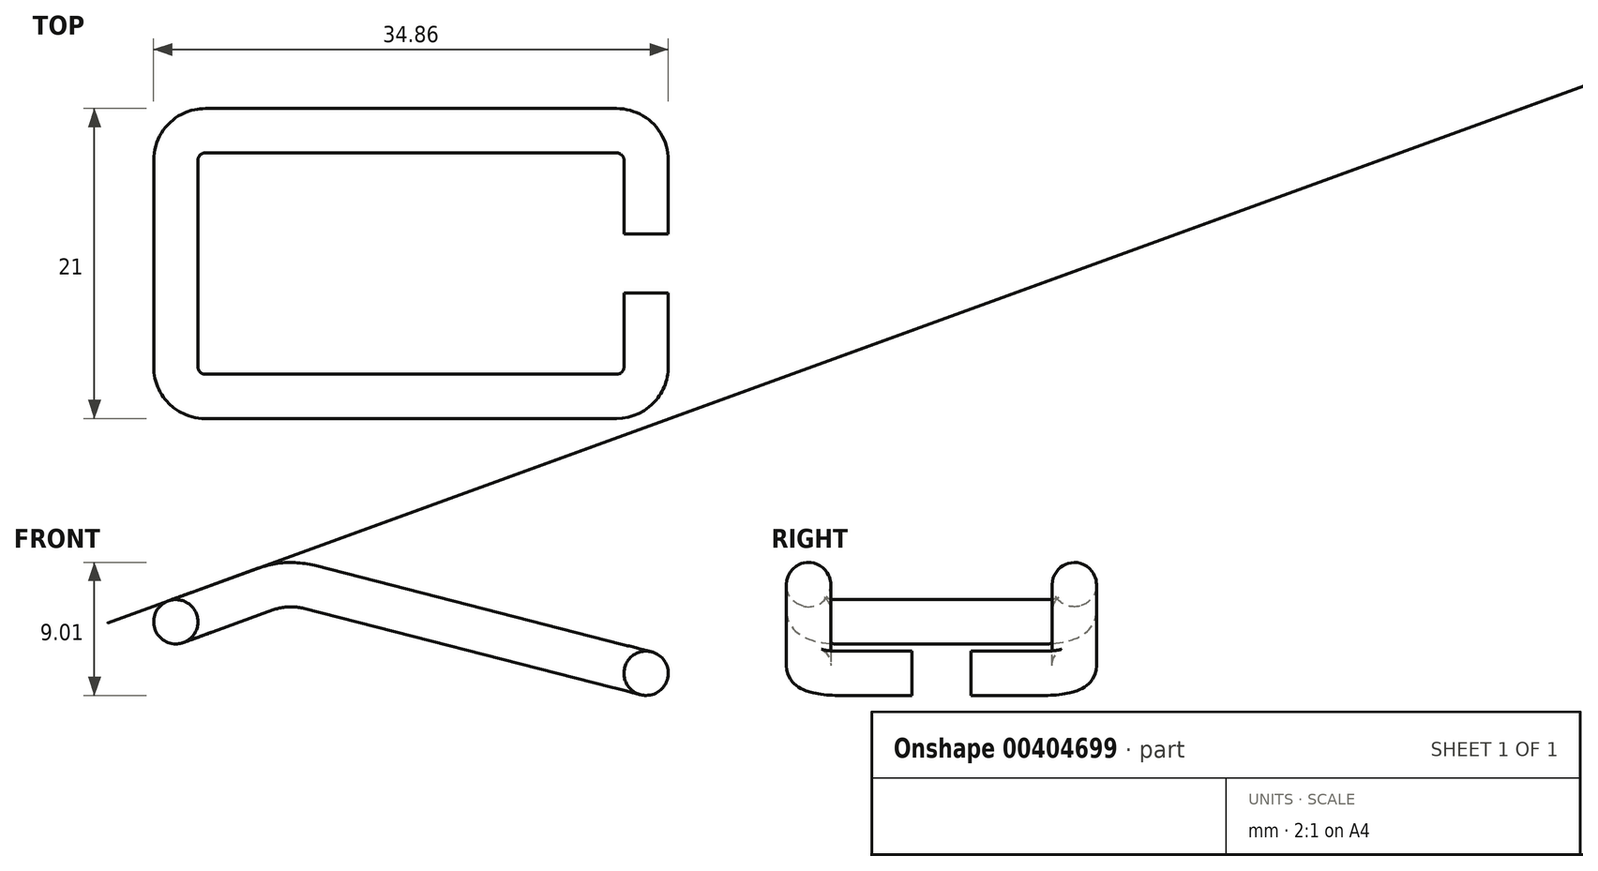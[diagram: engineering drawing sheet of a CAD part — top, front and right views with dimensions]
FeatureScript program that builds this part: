
annotation { "Feature Type Name" : "Feature", "Feature Type Description" : "" }
export const myFeature = defineFeature(function(context is Context, id is Id, definition is map)
    precondition{}
    {
        {
            var Q0;
            Q0=qCreatedBy(makeId("Front.planeOp"),FACE);
            var sketch = newSketch(context, id + "F0", { "sketchPlane" : qUnion([Q0])});
            skLineSegment(sketch, "E0", {"start": v(-7.54, 3.5) * mm, "end": v(0, 6.23) * mm});
            skLineSegment(sketch, "E1", {"start": v(24.32, 0) * mm, "end": v(0, 6.23) * mm});
            skPoint(sketch, "E2.orphan", {"position": v(24.8, -0.12) * mm});
            skLineSegment(sketch, "E3", {"start": v(24.32, 0) * mm, "end": v(-7.54, 0) * mm});
            skLineSegment(sketch, "E4", {"start": v(-7.54, 0) * mm, "end": v(-7.54, 3.5) * mm});
            skSolve(sketch);
        }
        {
            var Q0;
            Q0=makeQuery(id+"F0.imprint","IMPRINT",FACE,{"disambiguationData":[TD([[makeQuery(id+"F0.imprint","IMPRINT",EDGE,{"derivedFrom":sQuery(id+"F0.wireOp",EDGE,"E0")}),-1.0]])]});
            extrude(context, id + "F1", {"entities" : qUnion([Q0]), "oppositeDirection" : true, "depth" : 18 * mm, "symmetric" : true});
        }
        {
            var Q0;
            Q0=makeQuery(id+"F1.opExtrude","SWEPT_FACE",FACE,{"disambiguationData":[OSD([sQuery(id+"F0.wireOp",EDGE,"E1")])]});
            var sketch = newSketch(context, id + "F2", { "sketchPlane" : qUnion([Q0])});
            skLineSegment(sketch, "E5.bottom", {"start": v(21.7, 2) * mm, "end": v(25.41, 2) * mm});
            skLineSegment(sketch, "E5.top", {"start": v(21.7, -2) * mm, "end": v(25.41, -2) * mm});
            skLineSegment(sketch, "E5.left", {"start": v(21.7, 2) * mm, "end": v(21.7, -2) * mm});
            skLineSegment(sketch, "E5.right", {"start": v(25.41, 2) * mm, "end": v(25.41, -2) * mm});
            skPoint(sketch, "E5.middle", {"position": v(23.56, 0) * mm});
            skSolve(sketch);
        }
        {
            var Q0;
            Q0 = qSketchRegion(id + "F2", true);
            extrude(context, id + "F3", {"entities" : qUnion([Q0]), "operationType" : NewBodyOperationType.REMOVE, "endBound" : BoundingType.THROUGH_ALL, "oppositeDirection" : true, "depth" : 25 * mm});
        }
        {
            var Q0;
            Q0=makeQuery(id+"F3.boolean.opBoolean","COPY",FACE,{"derivedFrom":makeQuery(id+"F3.opExtrude","SWEPT_FACE",FACE,{"disambiguationData":[OSD([sQuery(id+"F2.wireOp",EDGE,"E5.bottom")])]})});
            var sketch = newSketch(context, id + "F4", { "sketchPlane" : qUnion([Q0])});
            skPoint(sketch, "E6.0", {"position": v(24.32, 0) * mm});
            skCircle(sketch, "E7", {"center": v(24.32, 0) * mm, "radius": 1.5 * mm});
            skSolve(sketch);
        }
        {
            var Q0;
            Q0=makeQuery(id+"F1.opExtrude","SWEPT_FACE",FACE,{"disambiguationData":[OSD([sQuery(id+"F0.wireOp",EDGE,"E3")])]});
            extrude(context, id + "F5", {"entities" : qUnion([Q0]), "operationType" : NewBodyOperationType.ADD, "depth" : 5 * mm});
        }
        {
            var Q0;
            Q0=makeQuery(id+"F1.opExtrude","SWEPT_EDGE",EDGE,{"disambiguationData":[OSD([sQuery(id+"F0.wireOp",EDGE,"E0"),sQuery(id+"F0.wireOp",EDGE,"E1")])]});
            fillet(context, id + "F6", {"entities" : qUnion([Q0]), "radius" : 5 * mm, "tangentPropagation" : true, "allowEdgeOverflow" : false});
        }
        {
            var Q0;
            Q0=makeQuery(id+"F1.opExtrude","CAP_EDGE",EDGE,{"disambiguationData":[OSD([sQuery(id+"F0.wireOp",EDGE,"E4")])],"isStart":true});
            var Q1;
            Q1=makeQuery(id+"F1.opExtrude","CAP_EDGE",EDGE,{"disambiguationData":[OSD([sQuery(id+"F0.wireOp",EDGE,"E4")])],"isStart":false});
            var Q2;
            {var subQ0=sQuery(id+"F0.wireOp",EDGE,"E3");var subQ1=sQuery(id+"F0.wireOp",EDGE,"E1");Q2=makeQuery(id+"F5.opExtrude","SWEPT_EDGE",EDGE,{"disambiguationData":[OSD([subQ1,subQ0]),TDD([makeQuery(id+"F1.opExtrude","CAP_VERTEX",VERTEX,{"disambiguationData":[OSD([subQ1,subQ0])],"isStart":true})])]});}
            var Q3;
            {var subQ0=sQuery(id+"F0.wireOp",EDGE,"E3");var subQ1=sQuery(id+"F0.wireOp",EDGE,"E1");Q3=makeQuery(id+"F5.opExtrude","SWEPT_EDGE",EDGE,{"disambiguationData":[OSD([subQ1,subQ0]),TDD([makeQuery(id+"F1.opExtrude","CAP_VERTEX",VERTEX,{"disambiguationData":[OSD([subQ1,subQ0])],"isStart":false})])]});}
            fillet(context, id + "F7", {"entities" : qUnion([Q0, Q1, Q2, Q3]), "radius" : 2 * mm, "tangentPropagation" : true, "allowEdgeOverflow" : false});
        }
        {
            var Q0;
            Q0 = qSketchRegion(id + "F4", true);
            var Q1;
            {var subQ0=sQuery(id+"F0.wireOp",EDGE,"E3");var subQ1=sQuery(id+"F0.wireOp",EDGE,"E1");var subQ2=makeQuery(id+"F3.boolean.opBoolean","SPLIT",EDGE,{"disambiguationData":[TD([makeQuery(id+"F3.opExtrude","SWEPT_FACE",FACE,{"disambiguationData":[OSD([sQuery(id+"F2.wireOp",EDGE,"E5.bottom")])]})])],"derivedFrom":makeQuery(id+"F1.opExtrude","SWEPT_EDGE",EDGE,{"disambiguationData":[OSD([subQ1,subQ0])]})});Q1=makeQuery(id+"F5.boolean.opBoolean","MERGE",EDGE,{"derivedFrom":[subQ2,makeQuery(id+"F5.opExtrude","CAP_EDGE",EDGE,{"disambiguationData":[OSD([subQ1,subQ0]),TDD([subQ2])],"isStart":true})]});}
            var Q2;
            {var subQ0=sQuery(id+"F0.wireOp",EDGE,"E1");var subQ1=sQuery(id+"F0.wireOp",EDGE,"E3");Q2=makeQuery(id+"F7.opFillet","BLEND_EDGE",EDGE,{"blendedFrom":[makeQuery(id+"F5.opExtrude","SWEPT_EDGE",EDGE,{"disambiguationData":[OSD([subQ0,subQ1]),TDD([makeQuery(id+"F1.opExtrude","CAP_VERTEX",VERTEX,{"disambiguationData":[OSD([subQ0,subQ1])],"isStart":false})])]}),makeQuery(id+"F1.opExtrude","SWEPT_FACE",FACE,{"disambiguationData":[OSD([subQ0])]})],"blendedInto":[makeQuery(id+"F1.opExtrude","SWEPT_FACE",FACE,{"disambiguationData":[OSD([subQ0])]})]});}
            var Q3;
            Q3=makeQuery(id+"F1.opExtrude","CAP_EDGE",EDGE,{"disambiguationData":[OSD([sQuery(id+"F0.wireOp",EDGE,"E1")])],"isStart":false});
            var Q4;
            {var subQ0=sQuery(id+"F0.wireOp",EDGE,"E3");var subQ1=sQuery(id+"F0.wireOp",EDGE,"E1");var subQ2=sQuery(id+"F0.wireOp",EDGE,"E0");Q4=makeQuery(id+"F6.opFillet","BLEND_EDGE",EDGE,{"blendedFrom":[makeQuery(id+"F1.opExtrude","SWEPT_EDGE",EDGE,{"disambiguationData":[OSD([subQ2,subQ1])]}),makeQuery(id+"F5.boolean.opBoolean","MERGE",FACE,{"derivedFrom":[makeQuery(id+"F1.opExtrude","CAP_FACE",FACE,{"disambiguationData":[OSD([subQ2,subQ1,subQ0,sQuery(id+"F0.wireOp",EDGE,"E4")])],"isStart":false}),makeQuery(id+"F5.opExtrude","SWEPT_FACE",FACE,{"disambiguationData":[OSD([subQ0]),TDD([makeQuery(id+"F1.opExtrude","CAP_EDGE",EDGE,{"disambiguationData":[OSD([subQ0])],"isStart":false})])]})]})],"blendedInto":[makeQuery(id+"F5.boolean.opBoolean","MERGE",FACE,{"derivedFrom":[makeQuery(id+"F1.opExtrude","CAP_FACE",FACE,{"disambiguationData":[OSD([subQ2,subQ1,subQ0,sQuery(id+"F0.wireOp",EDGE,"E4")])],"isStart":false}),makeQuery(id+"F5.opExtrude","SWEPT_FACE",FACE,{"disambiguationData":[OSD([subQ0]),TDD([makeQuery(id+"F1.opExtrude","CAP_EDGE",EDGE,{"disambiguationData":[OSD([subQ0])],"isStart":false})])]})]})]});}
            var Q5;
            Q5=makeQuery(id+"F1.opExtrude","CAP_EDGE",EDGE,{"disambiguationData":[OSD([sQuery(id+"F0.wireOp",EDGE,"E0")])],"isStart":false});
            var Q6;
            {var subQ0=sQuery(id+"F0.wireOp",EDGE,"E4");var subQ1=sQuery(id+"F0.wireOp",EDGE,"E3");Q6=makeQuery(id+"F7.opFillet","BLEND_EDGE",EDGE,{"blendedFrom":[makeQuery(id+"F5.boolean.opBoolean","MERGE",EDGE,{"derivedFrom":[makeQuery(id+"F1.opExtrude","CAP_EDGE",EDGE,{"disambiguationData":[OSD([subQ0])],"isStart":false}),makeQuery(id+"F5.opExtrude","SWEPT_EDGE",EDGE,{"disambiguationData":[OSD([subQ1,subQ0]),TDD([makeQuery(id+"F1.opExtrude","CAP_VERTEX",VERTEX,{"disambiguationData":[OSD([subQ1,subQ0])],"isStart":false})])]})]}),makeQuery(id+"F1.opExtrude","SWEPT_FACE",FACE,{"disambiguationData":[OSD([sQuery(id+"F0.wireOp",EDGE,"E0")])]})],"blendedInto":[makeQuery(id+"F1.opExtrude","SWEPT_FACE",FACE,{"disambiguationData":[OSD([sQuery(id+"F0.wireOp",EDGE,"E0")])]})]});}
            var Q7;
            Q7=makeQuery(id+"F1.opExtrude","SWEPT_EDGE",EDGE,{"disambiguationData":[OSD([sQuery(id+"F0.wireOp",EDGE,"E0"),sQuery(id+"F0.wireOp",EDGE,"E4")])]});
            var Q8;
            {var subQ0=sQuery(id+"F0.wireOp",EDGE,"E4");var subQ1=sQuery(id+"F0.wireOp",EDGE,"E3");Q8=makeQuery(id+"F7.opFillet","BLEND_EDGE",EDGE,{"blendedFrom":[makeQuery(id+"F5.boolean.opBoolean","MERGE",EDGE,{"derivedFrom":[makeQuery(id+"F1.opExtrude","CAP_EDGE",EDGE,{"disambiguationData":[OSD([subQ0])],"isStart":true}),makeQuery(id+"F5.opExtrude","SWEPT_EDGE",EDGE,{"disambiguationData":[OSD([subQ1,subQ0]),TDD([makeQuery(id+"F1.opExtrude","CAP_VERTEX",VERTEX,{"disambiguationData":[OSD([subQ1,subQ0])],"isStart":true})])]})]}),makeQuery(id+"F1.opExtrude","SWEPT_FACE",FACE,{"disambiguationData":[OSD([sQuery(id+"F0.wireOp",EDGE,"E0")])]})],"blendedInto":[makeQuery(id+"F1.opExtrude","SWEPT_FACE",FACE,{"disambiguationData":[OSD([sQuery(id+"F0.wireOp",EDGE,"E0")])]})]});}
            var Q9;
            Q9=makeQuery(id+"F1.opExtrude","CAP_EDGE",EDGE,{"disambiguationData":[OSD([sQuery(id+"F0.wireOp",EDGE,"E0")])],"isStart":true});
            var Q10;
            {var subQ0=sQuery(id+"F0.wireOp",EDGE,"E3");var subQ1=sQuery(id+"F0.wireOp",EDGE,"E1");var subQ2=sQuery(id+"F0.wireOp",EDGE,"E0");Q10=makeQuery(id+"F6.opFillet","BLEND_EDGE",EDGE,{"blendedFrom":[makeQuery(id+"F1.opExtrude","SWEPT_EDGE",EDGE,{"disambiguationData":[OSD([subQ2,subQ1])]}),makeQuery(id+"F5.boolean.opBoolean","MERGE",FACE,{"derivedFrom":[makeQuery(id+"F1.opExtrude","CAP_FACE",FACE,{"disambiguationData":[OSD([subQ2,subQ1,subQ0,sQuery(id+"F0.wireOp",EDGE,"E4")])],"isStart":true}),makeQuery(id+"F5.opExtrude","SWEPT_FACE",FACE,{"disambiguationData":[OSD([subQ0]),TDD([makeQuery(id+"F1.opExtrude","CAP_EDGE",EDGE,{"disambiguationData":[OSD([subQ0])],"isStart":true})])]})]})],"blendedInto":[makeQuery(id+"F5.boolean.opBoolean","MERGE",FACE,{"derivedFrom":[makeQuery(id+"F1.opExtrude","CAP_FACE",FACE,{"disambiguationData":[OSD([subQ2,subQ1,subQ0,sQuery(id+"F0.wireOp",EDGE,"E4")])],"isStart":true}),makeQuery(id+"F5.opExtrude","SWEPT_FACE",FACE,{"disambiguationData":[OSD([subQ0]),TDD([makeQuery(id+"F1.opExtrude","CAP_EDGE",EDGE,{"disambiguationData":[OSD([subQ0])],"isStart":true})])]})]})]});}
            var Q11;
            Q11=makeQuery(id+"F1.opExtrude","CAP_EDGE",EDGE,{"disambiguationData":[OSD([sQuery(id+"F0.wireOp",EDGE,"E1")])],"isStart":true});
            var Q12;
            {var subQ0=sQuery(id+"F0.wireOp",EDGE,"E1");var subQ1=sQuery(id+"F0.wireOp",EDGE,"E3");Q12=makeQuery(id+"F7.opFillet","BLEND_EDGE",EDGE,{"blendedFrom":[makeQuery(id+"F5.opExtrude","SWEPT_EDGE",EDGE,{"disambiguationData":[OSD([subQ0,subQ1]),TDD([makeQuery(id+"F1.opExtrude","CAP_VERTEX",VERTEX,{"disambiguationData":[OSD([subQ0,subQ1])],"isStart":true})])]}),makeQuery(id+"F1.opExtrude","SWEPT_FACE",FACE,{"disambiguationData":[OSD([subQ0])]})],"blendedInto":[makeQuery(id+"F1.opExtrude","SWEPT_FACE",FACE,{"disambiguationData":[OSD([subQ0])]})]});}
            var Q13;
            {var subQ0=sQuery(id+"F0.wireOp",EDGE,"E3");var subQ1=sQuery(id+"F0.wireOp",EDGE,"E1");var subQ2=makeQuery(id+"F3.boolean.opBoolean","SPLIT",EDGE,{"disambiguationData":[TD([makeQuery(id+"F3.opExtrude","SWEPT_FACE",FACE,{"disambiguationData":[OSD([sQuery(id+"F2.wireOp",EDGE,"E5.top")])]})])],"derivedFrom":makeQuery(id+"F1.opExtrude","SWEPT_EDGE",EDGE,{"disambiguationData":[OSD([subQ1,subQ0])]})});Q13=makeQuery(id+"F5.boolean.opBoolean","MERGE",EDGE,{"derivedFrom":[subQ2,makeQuery(id+"F5.opExtrude","CAP_EDGE",EDGE,{"disambiguationData":[OSD([subQ1,subQ0]),TDD([subQ2])],"isStart":true})]});}
            sweep(context, id + "F8", {"profiles" : qUnion([Q0]), "path" : qUnion([Q1, Q2, Q3, Q4, Q5, Q6, Q7, Q8, Q9, Q10, Q11, Q12, Q13])});
        }
        {
            var Q0;
            Q0=makeQuery(id+"F1.opExtrude","SWEPT_BODY",BODY,{"disambiguationData":[OSD([sQuery(id+"F0.wireOp",EDGE,"E0"),sQuery(id+"F0.wireOp",EDGE,"E1"),sQuery(id+"F0.wireOp",EDGE,"E3"),sQuery(id+"F0.wireOp",EDGE,"E4")])]});
            deleteBodies(context, id + "F9", {"entities" : qUnion([Q0])});
        }
    });
